annotation { "Feature Type Name" : "Feature", "Feature Type Description" : "" }
export const myFeature = defineFeature(function(context is Context, id is Id, definition is map)
    precondition{}
    {
        {
            var Q0;
            Q0=qCreatedBy(makeId("Front.planeOp"),FACE);
            var sketch = newSketch(context, id + "F0", { "sketchPlane" : qUnion([Q0])});
            skCircle(sketch, "E0", {"center": v(0, 0) * mm, "radius": 304.8 * mm});
            skLineSegment(sketch, "E1", {"start": v(0, 0) * mm, "end": v(609.6, 0) * mm});
            skLineSegment(sketch, "E2", {"start": v(0, 0) * mm, "end": v(0, 609.6) * mm});
            skLineSegment(sketch, "E3.MirrorCS", {"start": v(0, 0) * mm, "end": v(-609.6, 0) * mm});
            skLineSegment(sketch, "E4", {"start": v(0, 0) * mm, "end": v(460.7, 242.32) * mm});
            skLineSegment(sketch, "E5", {"start": v(609.6, 152.4) * mm, "end": v(609.6, -152.4) * mm});
            skLineSegment(sketch, "E6", {"start": v(0, 0) * mm, "end": v(460.7, -242.32) * mm});
            skPoint(sketch, "E7.visualSharp", {"position": v(609.6, 320.64) * mm});
            skArc(sketch, "E7.filletArc", {"start": v(609.6, 152.4) * mm, "mid": v(560.52, 239.37) * mm, "end": v(460.7, 242.32) * mm});
            skPoint(sketch, "E8.visualSharp", {"position": v(609.6, -320.64) * mm});
            skArc(sketch, "E8.filletArc", {"start": v(460.7, -242.32) * mm, "mid": v(560.52, -239.37) * mm, "end": v(609.6, -152.4) * mm});
            skLineSegment(sketch, "E9", {"start": v(0, 0) * mm, "end": v(-242.32, 460.7) * mm});
            skLineSegment(sketch, "E10", {"start": v(-152.4, 609.6) * mm, "end": v(152.4, 609.6) * mm});
            skLineSegment(sketch, "E11", {"start": v(242.32, 460.7) * mm, "end": v(0, 0) * mm});
            skPoint(sketch, "E12.visualSharp", {"position": v(-320.64, 609.6) * mm});
            skArc(sketch, "E12.filletArc", {"start": v(-152.4, 609.6) * mm, "mid": v(-239.37, 560.52) * mm, "end": v(-242.32, 460.7) * mm});
            skPoint(sketch, "E13.visualSharp", {"position": v(320.64, 609.6) * mm});
            skArc(sketch, "E13.filletArc", {"start": v(242.32, 460.7) * mm, "mid": v(239.37, 560.52) * mm, "end": v(152.4, 609.6) * mm});
            skLineSegment(sketch, "E14.MirrorCS", {"start": v(0, 0) * mm, "end": v(-460.7, 242.32) * mm});
            skArc(sketch, "E15.MirrorCS", {"start": v(-609.6, 152.4) * mm, "mid": v(-560.52, 239.37) * mm, "end": v(-460.7, 242.32) * mm});
            skLineSegment(sketch, "E16.MirrorCS", {"start": v(-609.6, 152.4) * mm, "end": v(-609.6, -152.4) * mm});
            skArc(sketch, "E17.MirrorCS", {"start": v(-460.7, -242.32) * mm, "mid": v(-560.52, -239.37) * mm, "end": v(-609.6, -152.4) * mm});
            skLineSegment(sketch, "E18.MirrorCS", {"start": v(0, 0) * mm, "end": v(-460.7, -242.32) * mm});
            skLineSegment(sketch, "E19", {"start": v(0, 0) * mm, "end": v(0, -1219.2) * mm});
            skLineSegment(sketch, "E20", {"start": v(-228.6, -1219.2) * mm, "end": v(228.6, -1219.2) * mm});
            skLineSegment(sketch, "E21", {"start": v(-228.6, -1219.2) * mm, "end": v(-152.4, 0) * mm});
            skLineSegment(sketch, "E22", {"start": v(-152.4, 0) * mm, "end": v(152.4, 0) * mm});
            skLineSegment(sketch, "E23", {"start": v(152.4, 0) * mm, "end": v(228.6, -1219.2) * mm});
            skSolve(sketch);
        }
        {
            var Q0;
            Q0 = qSketchRegion(id + "F0", true);
            var Q1;
            {var subQ1=sQuery(id+"F0.wireOp",EDGE,"E6");var subQ3=sQuery(id+"F0.wireOp",EDGE,"E23");var subQ4=makeQuery(id+"F0.imprint","INTERSECT",VERTEX,{"derivedFrom":[subQ1,subQ3]});Q1=makeQuery(id+"F0.imprint","IMPRINT",FACE,{"disambiguationData":[TD([[makeQuery(id+"F0.imprint","IMPRINT",EDGE,{"disambiguationData":[TD([[subQ4,1.0]])],"derivedFrom":subQ3}),-1.0]])]});}
            var Q2;
            {var subQ1=sQuery(id+"F0.wireOp",EDGE,"E18.MirrorCS");var subQ3=sQuery(id+"F0.wireOp",EDGE,"E21");var subQ4=makeQuery(id+"F0.imprint","INTERSECT",VERTEX,{"derivedFrom":[subQ1,subQ3]});Q2=makeQuery(id+"F0.imprint","IMPRINT",FACE,{"disambiguationData":[TD([[makeQuery(id+"F0.imprint","IMPRINT",EDGE,{"disambiguationData":[TD([[subQ4,-1.0]])],"derivedFrom":subQ3}),-1.0]])]});}
            extrude(context, id + "F1", {"entities" : qUnion([Q0, Q1, Q2]), "depth" : 304.8 * mm});
        }
        {
            var Q0;
            Q0=makeQuery(id+"F1.opExtrude","CAP_FACE",FACE,{"disambiguationData":[OSD([sQuery(id+"F0.wireOp",EDGE,"E0"),sQuery(id+"F0.wireOp",EDGE,"E4"),sQuery(id+"F0.wireOp",EDGE,"E5"),sQuery(id+"F0.wireOp",EDGE,"E6"),sQuery(id+"F0.wireOp",EDGE,"E7.filletArc"),sQuery(id+"F0.wireOp",EDGE,"E8.filletArc"),sQuery(id+"F0.wireOp",EDGE,"E9"),sQuery(id+"F0.wireOp",EDGE,"E10"),sQuery(id+"F0.wireOp",EDGE,"E11"),sQuery(id+"F0.wireOp",EDGE,"E12.filletArc"),sQuery(id+"F0.wireOp",EDGE,"E13.filletArc"),sQuery(id+"F0.wireOp",EDGE,"E14.MirrorCS"),sQuery(id+"F0.wireOp",EDGE,"E15.MirrorCS"),sQuery(id+"F0.wireOp",EDGE,"E16.MirrorCS"),sQuery(id+"F0.wireOp",EDGE,"E17.MirrorCS"),sQuery(id+"F0.wireOp",EDGE,"E18.MirrorCS"),sQuery(id+"F0.wireOp",EDGE,"E20"),sQuery(id+"F0.wireOp",EDGE,"E21"),sQuery(id+"F0.wireOp",EDGE,"E23")])],"isStart":false});
            var sketch = newSketch(context, id + "F2", { "sketchPlane" : qUnion([Q0])});
            skText(sketch, "E24", { "text": "\nR. I. P.\n", "fontName": "NotoSansCJKjp-Regular.otf"});
            skText(sketch, "E25", { "text": "Jacob Harmon", "fontName": "OpenSans-Regular.ttf"});
            const initialGuessF2  = {"E24": [-0.29265, 0.16287, 1, 0, 0.15026], "E25": [-0.237, -0.10398, 1, 0, 0.04121]};
            skSetInitialGuess(sketch, initialGuessF2);
            skSolve(sketch);
        }
        {
            var Q0;
            Q0 = qSketchRegion(id + "F2", true);
            extrude(context, id + "F3", {"entities" : qUnion([Q0]), "operationType" : NewBodyOperationType.REMOVE, "oppositeDirection" : true, "depth" : 25.4 * mm});
        }
    });